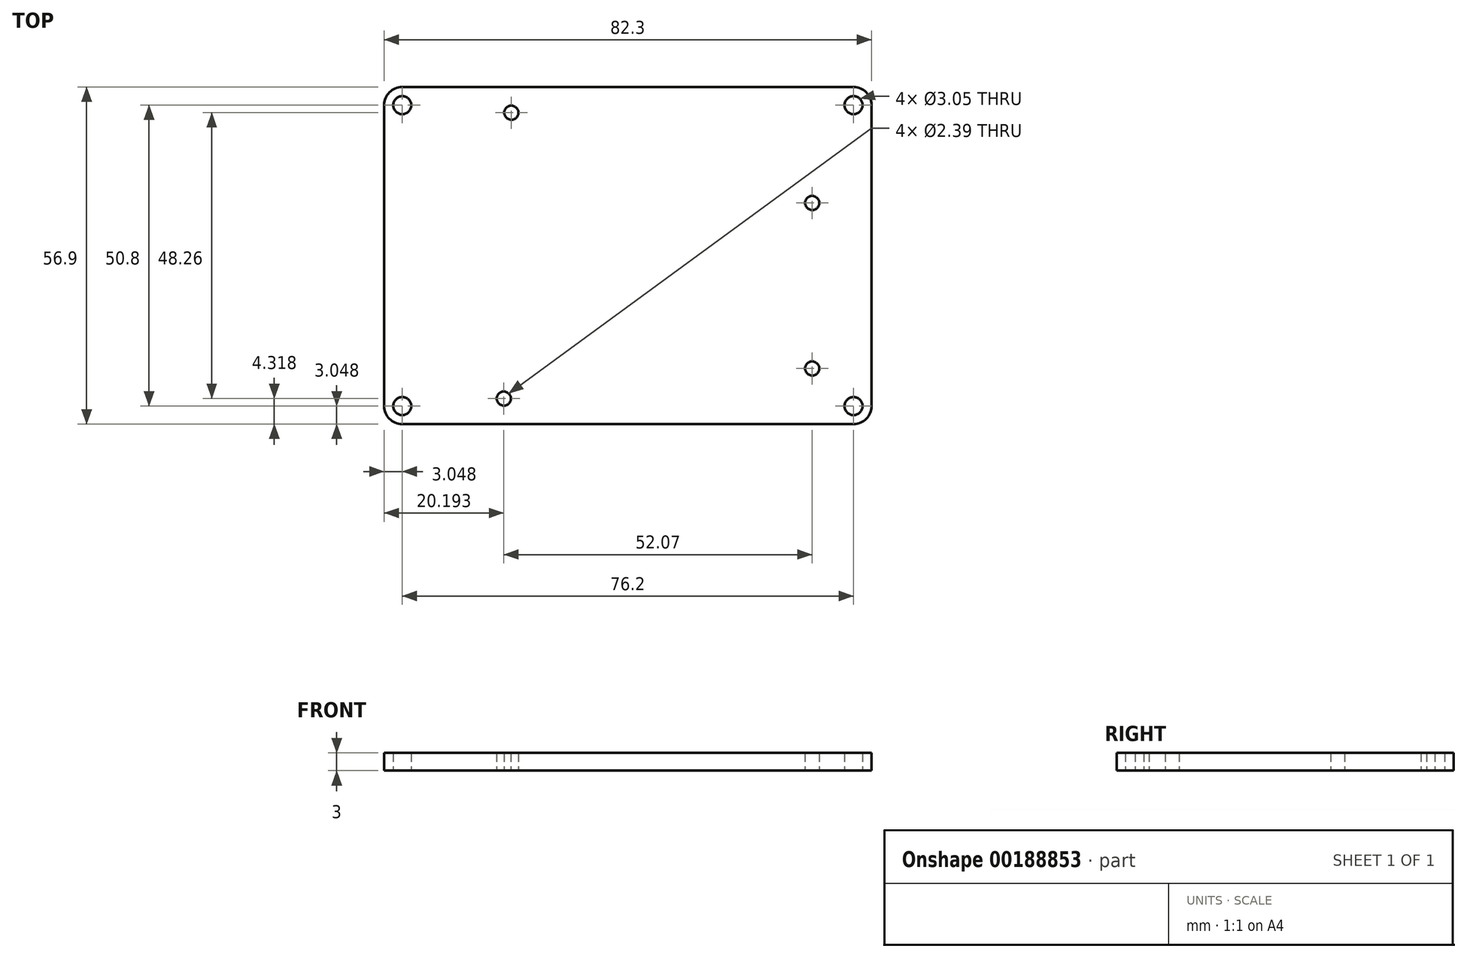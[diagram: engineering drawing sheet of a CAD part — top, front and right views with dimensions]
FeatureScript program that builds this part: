
annotation { "Feature Type Name" : "Feature", "Feature Type Description" : "" }
export const myFeature = defineFeature(function(context is Context, id is Id, definition is map)
    precondition{}
    {
        {
            var Q0;
            Q0=qCreatedBy(makeId("Top.planeOp"),FACE);
            var sketch = newSketch(context, id + "F0", { "sketchPlane" : qUnion([Q0])});
            skLineSegment(sketch, "E0.bottom", {"start": v(3.05, 0) * mm, "end": v(79.25, 0) * mm});
            skLineSegment(sketch, "E0.top", {"start": v(3.05, 56.9) * mm, "end": v(79.25, 56.9) * mm});
            skLineSegment(sketch, "E0.left", {"start": v(0, 3.05) * mm, "end": v(0, 53.85) * mm});
            skLineSegment(sketch, "E0.right", {"start": v(82.3, 3.05) * mm, "end": v(82.3, 53.85) * mm});
            skCircle(sketch, "E1", {"center": v(3.05, 3.05) * mm, "radius": 1.52 * mm});
            skCircle(sketch, "E2", {"center": v(3.05, 53.85) * mm, "radius": 1.52 * mm});
            skCircle(sketch, "E3", {"center": v(79.25, 53.85) * mm, "radius": 1.52 * mm});
            skCircle(sketch, "E4", {"center": v(79.25, 3.05) * mm, "radius": 1.52 * mm});
            skCircle(sketch, "E5", {"center": v(21.46, 52.58) * mm, "radius": 1.2 * mm});
            skCircle(sketch, "E6", {"center": v(20.2, 4.32) * mm, "radius": 1.2 * mm});
            skCircle(sketch, "E7", {"center": v(72.26, 9.4) * mm, "radius": 1.2 * mm});
            skCircle(sketch, "E8", {"center": v(72.26, 37.34) * mm, "radius": 1.2 * mm});
            skPoint(sketch, "E9.visualSharp", {"position": v(0, 56.9) * mm});
            skArc(sketch, "E9.filletArc", {"start": v(3.05, 56.9) * mm, "mid": v(0.9, 56) * mm, "end": v(0, 53.85) * mm});
            skPoint(sketch, "E10.visualSharp", {"position": v(82.3, 56.9) * mm});
            skArc(sketch, "E10.filletArc", {"start": v(82.3, 53.85) * mm, "mid": v(81.4, 56) * mm, "end": v(79.25, 56.9) * mm});
            skPoint(sketch, "E11.visualSharp", {"position": v(82.3, 0) * mm});
            skArc(sketch, "E11.filletArc", {"start": v(79.25, 0) * mm, "mid": v(81.4, 0.9) * mm, "end": v(82.3, 3.05) * mm});
            skPoint(sketch, "E12.visualSharp", {"position": v(0, 0) * mm});
            skArc(sketch, "E12.filletArc", {"start": v(0, 3.05) * mm, "mid": v(0.9, 0.9) * mm, "end": v(3.05, 0) * mm});
            skSolve(sketch);
        }
        {
            var Q0;
            Q0 = qSketchRegion(id + "F0", true);
            extrude(context, id + "F1", {"entities" : qUnion([Q0]), "depth" : 3 * mm});
        }
    });
